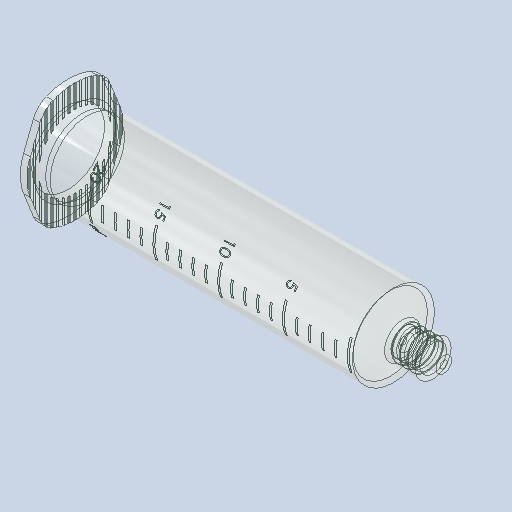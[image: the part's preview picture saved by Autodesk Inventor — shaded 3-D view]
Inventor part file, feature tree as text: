
AUTODESK INVENTOR PART (.ipt)
format: ipt  version: 2025.2 (Build 292293000, 293)  size: 1,581,056 bytes
history: native  units: in
note: dims shown in document units (in); Inventor stores cm internally (conversion verified against a paired STEP export)
features: thread x1
ambient origin geometry x8: Origin, YZ Plane, XZ Plane, XY Plane, X Axis, Y Axis, Z Axis, Center Point
bodies: Solid1 (feature_tree)
feature tree (1):
  thread  "Thread1"  [1 undecoded]
note: 1 required parameter value undecoded (feature->parameter linkage not recoverable at this tier; creation-order binding heuristic only, values carry confidence <= 0.55)
